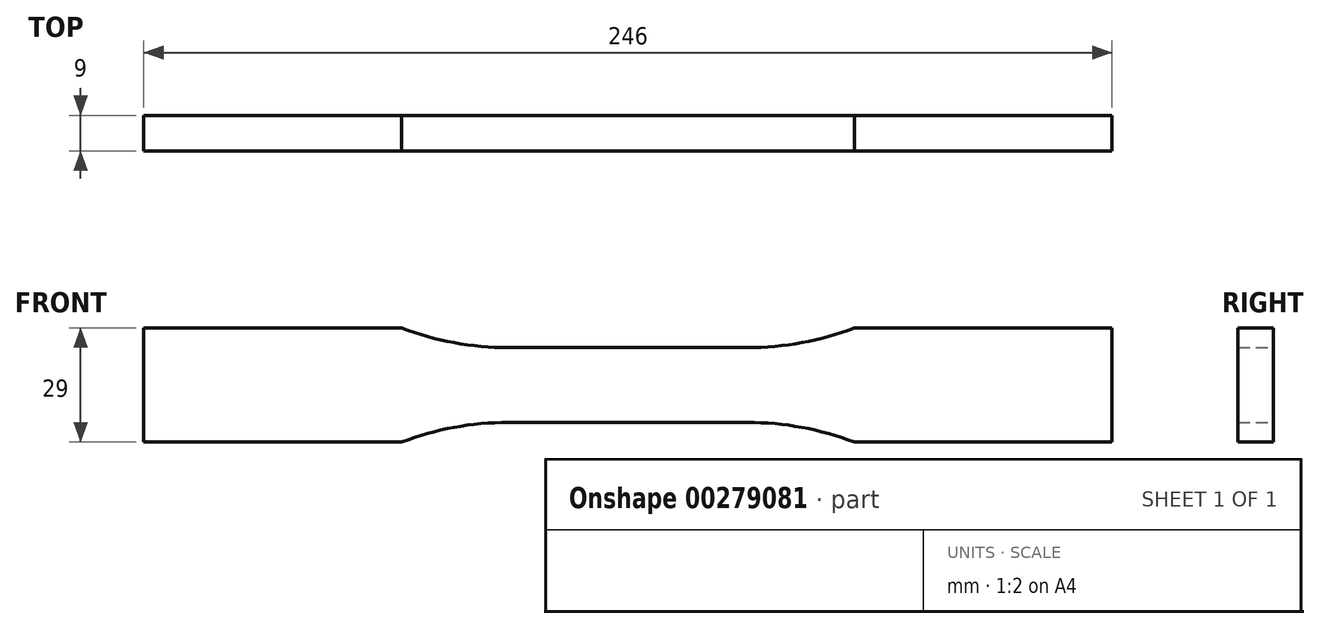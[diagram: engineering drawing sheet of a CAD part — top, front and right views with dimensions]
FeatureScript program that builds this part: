
annotation { "Feature Type Name" : "Feature", "Feature Type Description" : "" }
export const myFeature = defineFeature(function(context is Context, id is Id, definition is map)
    precondition{}
    {
        {
            var Q0;
            Q0=qCreatedBy(makeId("Front.planeOp"),FACE);
            var sketch = newSketch(context, id + "F0", { "sketchPlane" : qUnion([Q0])});
            skLineSegment(sketch, "E0", {"start": v(0, 9.5) * mm, "end": v(30.39, 9.5) * mm});
            skArc(sketch, "E1", {"start": v(30.39, 9.5) * mm, "mid": v(44.17, 10.76) * mm, "end": v(57.5, 14.5) * mm});
            skLineSegment(sketch, "E2", {"start": v(57.5, 14.5) * mm, "end": v(123, 14.5) * mm});
            skLineSegment(sketch, "E3.MirrorCS", {"start": v(57.5, -14.5) * mm, "end": v(123, -14.5) * mm});
            skLineSegment(sketch, "E4.MirrorCS", {"start": v(0, -9.5) * mm, "end": v(30.39, -9.5) * mm});
            skArc(sketch, "E5.MirrorCS", {"start": v(30.39, -9.5) * mm, "mid": v(44.17, -10.76) * mm, "end": v(57.5, -14.5) * mm});
            skLineSegment(sketch, "E6.MirrorCS", {"start": v(0, -9.5) * mm, "end": v(-30.39, -9.5) * mm});
            skLineSegment(sketch, "E7.MirrorCS", {"start": v(-57.5, -14.5) * mm, "end": v(-123, -14.5) * mm});
            skLineSegment(sketch, "E8.MirrorCS", {"start": v(0, 9.5) * mm, "end": v(-30.39, 9.5) * mm});
            skLineSegment(sketch, "E9.MirrorCS", {"start": v(-57.5, 14.5) * mm, "end": v(-123, 14.5) * mm});
            skArc(sketch, "E10.MirrorCS", {"start": v(-30.39, -9.5) * mm, "mid": v(-44.17, -10.76) * mm, "end": v(-57.5, -14.5) * mm});
            skArc(sketch, "E11.MirrorCS", {"start": v(-30.39, 9.5) * mm, "mid": v(-44.17, 10.76) * mm, "end": v(-57.5, 14.5) * mm});
            skLineSegment(sketch, "E12", {"start": v(-123, 14.5) * mm, "end": v(-123, -14.5) * mm});
            skLineSegment(sketch, "E13", {"start": v(123, 14.5) * mm, "end": v(123, -14.5) * mm});
            skSolve(sketch);
        }
        {
            var Q0;
            Q0 = qSketchRegion(id + "F0", true);
            extrude(context, id + "F1", {"entities" : qUnion([Q0]), "endBound" : BoundingType.SYMMETRIC, "depth" : 9 * mm});
        }
    });
